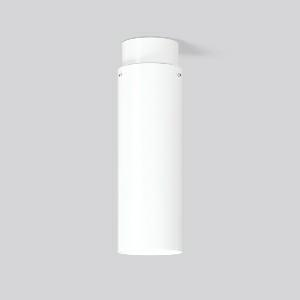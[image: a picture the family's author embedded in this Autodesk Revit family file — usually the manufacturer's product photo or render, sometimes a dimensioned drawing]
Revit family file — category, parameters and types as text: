
# Revit family: glasdownlight_931180_002_9889
name_source: partatom
category: Lighting Fixtures
units: mm (PartAtom-declared; Revit-internal decimal feet)

## family parameters
Cut with Voids When Loaded = No
Host = Face
Light Source = No
Part Type = Normal
Room Calculation Point = No
Round Connector Dimension = Use Diameter
Shared = No

## types (1)
- GLASDOWNLIGHT (1 x LED Modul 830, 2600 lm, 3000)
    Apparent Load = 20 VA
    CIE Flux Codes = 22 47 73 55 100
    Color Rendering = 80
    Color Temperature = 3000
    Default Elevation = 1800 mm
    Description = Series: GLASDOWNLIGHT
Decorative round surface-mounted luminaire. Base: aluminium, powder-coated. Mouth blown 3-layer opal glass (Triplex glass) with satin finish. Glass fastening: retaining screws. Triplex glass produces particularly homogeneous, soft and glare free lighting. 
Colour: white
Diameter: 150 mm
Height: 470 mm
Lamp: LED
Socket: without socket
Colour temperature: 3000K
Colour rendering index (CRI): 80
System power: 20 W
Rated luminous flux: 2600 lm
Luminous efficiency: 130 lm/W
Control gear: Regulated power supply
Protection class: I
Type of protection: IP 20
    Height = 470 mm
    Lamp = 1 x LED Modul 830
    Lamp Light Flux = 2600 lm
    Lamp count = 1
    Length = 150 mm
    Lifetime = 50000 h
    Luminous efficacy = 130 lm/W
    Manufacturer = RZB
    ModVariant = No
    Model = 931180.002
    Mounting Place = Ceiling
    Mounting Type = Surface mounted
    Number of Poles = 1
    OnlyDefault = Yes
    Power Factor = 1
    Product Name = GLASDOWNLIGHT
    Product group = Surface mounted ceiling luminaires
    ProductGroupID = 303
    Protection Class = Protection class I
    Protection Degree = IP 20
    RLX_Detail_Level = 1
    RLX_Emergency_Light_Flux = 0 lm
    RLX_Emergency_Type = 0
    RLX_Emergency_Type_DB = No
    RlxData = <blob elided: 15429 chars, md5=ce57d0f2>
    Socket = socket
    Standby Power = 0 W
    System Light Flux = 2600 lm
    System Power = 20 W
    Type Comments = Product without accessories
    Type Image = 931180.002.jpg
    URL = http://relux.com
    VarID = ---
    Voltage = 230 V
    Voltage Range = 220-240 V
    Weight = 0.00 kg
    Width = 0 mm  [stored 0 ft]

note: [stored X ft] marks values corroborated as IEEE doubles in the binary element streams (Revit-internal decimal feet)

## geometry (parser evidence)
native form markers: Sweep x12
no freeform markers — native parametric forms only
